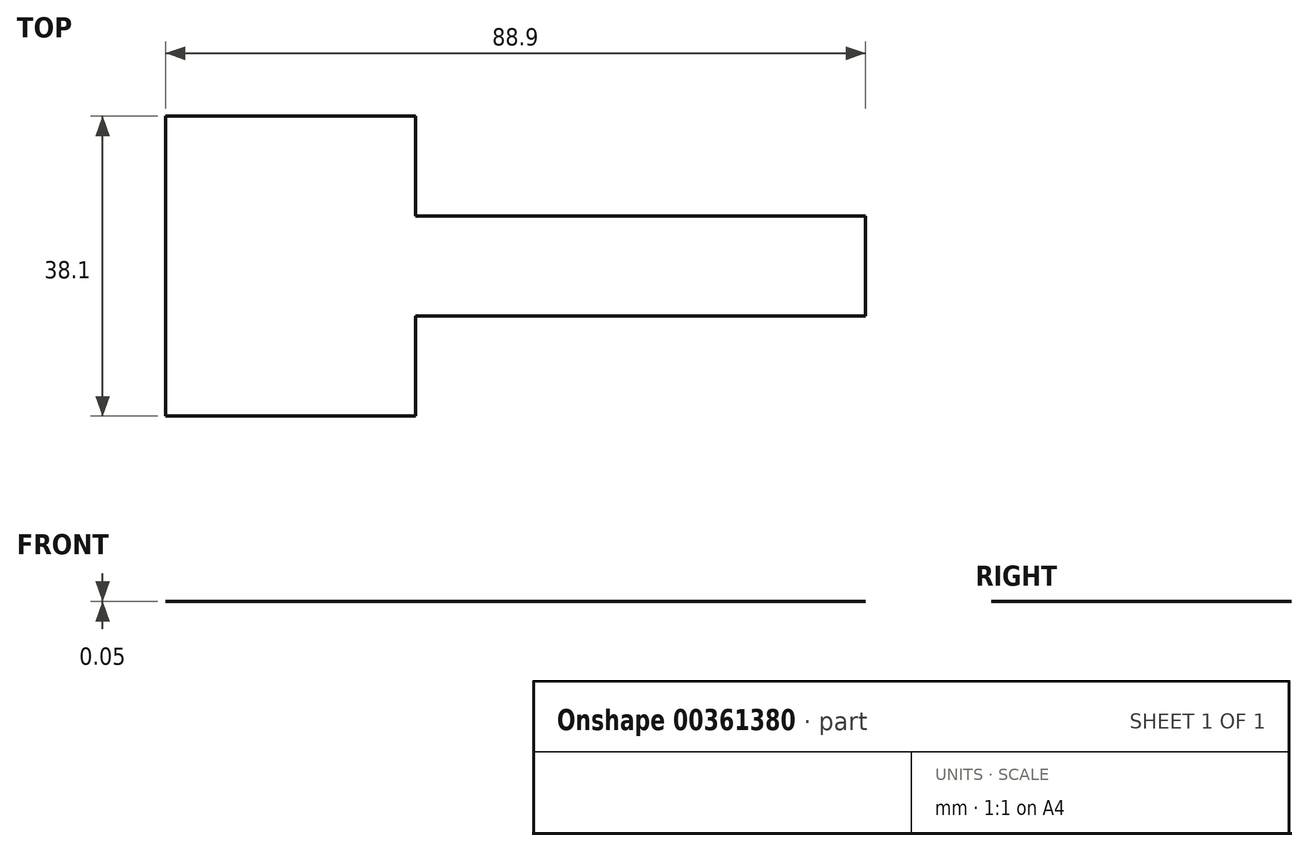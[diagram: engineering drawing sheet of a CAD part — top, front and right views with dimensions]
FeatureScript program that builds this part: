
annotation { "Feature Type Name" : "Feature", "Feature Type Description" : "" }
export const myFeature = defineFeature(function(context is Context, id is Id, definition is map)
    precondition{}
    {
        {
            var Q0;
            Q0=qCreatedBy(makeId("Top.planeOp"),FACE);
            var sketch = newSketch(context, id + "F0", { "sketchPlane" : qUnion([Q0])});
            skLineSegment(sketch, "E0", {"start": v(-91.66, -16.6) * mm, "end": v(-91.66, -54.7) * mm});
            skLineSegment(sketch, "E1", {"start": v(-91.66, -54.7) * mm, "end": v(-59.91, -54.7) * mm});
            skLineSegment(sketch, "E2", {"start": v(-59.91, -54.7) * mm, "end": v(-59.91, -42) * mm});
            skLineSegment(sketch, "E3", {"start": v(-59.91, -42) * mm, "end": v(-2.76, -42) * mm});
            skLineSegment(sketch, "E4", {"start": v(-2.76, -42) * mm, "end": v(-2.76, -29.3) * mm});
            skLineSegment(sketch, "E5", {"start": v(-2.76, -29.3) * mm, "end": v(-59.91, -29.3) * mm});
            skLineSegment(sketch, "E6", {"start": v(-59.91, -29.3) * mm, "end": v(-59.91, -16.6) * mm});
            skLineSegment(sketch, "E7", {"start": v(-59.91, -16.6) * mm, "end": v(-91.66, -16.6) * mm});
            skSolve(sketch);
        }
        {
            var Q0;
            Q0 = qSketchRegion(id + "F0", true);
            extrude(context, id + "F1", {"entities" : qUnion([Q0]), "depth" : 5 / 101.6 * mm});
        }
        {
            var Q0;
            Q0=makeQuery(id+"F1.opExtrude","SWEPT_FACE",FACE,{"disambiguationData":[OSD([sQuery(id+"F0.wireOp",EDGE,"E1")])]});
            var sketch = newSketch(context, id + "F2", { "sketchPlane" : qUnion([Q0])});
            skLineSegment(sketch, "E8", {"start": v(-59.91, 0) * mm, "end": v(-74.42, 31.75) * mm});
            skLineSegment(sketch, "E9", {"start": v(-74.42, 31.75) * mm, "end": v(-59.91, 44.04) * mm});
            skLineSegment(sketch, "E10", {"start": v(-59.91, 44.04) * mm, "end": v(-48.71, 44.04) * mm});
            skLineSegment(sketch, "E11", {"start": v(-48.71, 44.04) * mm, "end": v(-48.71, 10.05) * mm});
            skLineSegment(sketch, "E12", {"start": v(-47.29, 10.05) * mm, "end": v(-59.91, 0) * mm});
            skSolve(sketch);
        }
        {
            var Q0;
            {var subQ0=sQuery(id+"F2.wireOp",EDGE,"E8");Q0=makeQuery(id+"F2.imprint","IMPRINT",FACE,{"disambiguationData":[TD([[makeQuery(id+"F2.imprint","IMPRINT",EDGE,{"derivedFrom":subQ0}),-1.0]])]});}
            extrude(context, id + "F3", {"entities" : qUnion([Q0]), "operationType" : NewBodyOperationType.REMOVE, "depth" : 25.4 * mm});
        }
        {
            var Q0;
            Q0=makeQuery(id+"F1.opExtrude","SWEPT_FACE",FACE,{"disambiguationData":[OSD([sQuery(id+"F0.wireOp",EDGE,"E1")])]});
            var sketch = newSketch(context, id + "F4", { "sketchPlane" : qUnion([Q0])});
            skLineSegment(sketch, "E13", {"start": v(-59.91, 0) * mm, "end": v(-75.79, 31.75) * mm});
            skLineSegment(sketch, "E14", {"start": v(-75.79, 31.75) * mm, "end": v(-62.04, 45.95) * mm});
            skLineSegment(sketch, "E15", {"start": v(-62.04, 45.95) * mm, "end": v(-46.33, 45.95) * mm});
            skLineSegment(sketch, "E16", {"start": v(-46.33, 45.95) * mm, "end": v(-46.33, 12.06) * mm});
            skLineSegment(sketch, "E17", {"start": v(-59.91, 0) * mm, "end": v(-46.33, 12.06) * mm});
            skSolve(sketch);
        }
        {
            var Q0;
            Q0 = qSketchRegion(id + "F4", true);
            extrude(context, id + "F5", {"entities" : qUnion([Q0]), "operationType" : NewBodyOperationType.REMOVE, "oppositeDirection" : true, "depth" : 12.7 * mm});
        }
        {
            var Q0;
            Q0=makeQuery(id+"F1.opExtrude","SWEPT_FACE",FACE,{"disambiguationData":[OSD([sQuery(id+"F0.wireOp",EDGE,"E7")])]});
            var sketch = newSketch(context, id + "F6", { "sketchPlane" : qUnion([Q0])});
            skLineSegment(sketch, "E18", {"start": v(72.61, 31.75) * mm, "end": v(59.91, 0) * mm});
            skSolve(sketch);
        }
        {
            var Q0;
            Q0 = qSketchRegion(id + "F6", true);
            var Q1;
            {var subQ0=sQuery(id+"F6.wireOp",EDGE,"E18");Q1=makeQuery(id+"F6.imprint","IMPRINT",FACE,{"disambiguationData":[TD([[makeQuery(id+"F6.imprint","IMPRINT",EDGE,{"derivedFrom":subQ0}),-1.0]])]});}
            extrude(context, id + "F7", {"entities" : qUnion([Q0, Q1]), "operationType" : NewBodyOperationType.REMOVE, "oppositeDirection" : true, "depth" : 12.7 * mm});
        }
        {
            var Q0;
            Q0=makeQuery(id+"F5.boolean.opBoolean","MERGE",FACE,{"derivedFrom":[makeQuery(id+"F1.opExtrude","SWEPT_FACE",FACE,{"disambiguationData":[OSD([sQuery(id+"F0.wireOp",EDGE,"E3")])]}),makeQuery(id+"F5.opExtrude","CAP_FACE",FACE,{"disambiguationData":[OSD([sQuery(id+"F4.wireOp",EDGE,"E13"),sQuery(id+"F4.wireOp",EDGE,"E14"),sQuery(id+"F4.wireOp",EDGE,"E15"),sQuery(id+"F4.wireOp",EDGE,"E16"),sQuery(id+"F4.wireOp",EDGE,"E17")])],"isStart":false})]});
            var sketch = newSketch(context, id + "F8", { "sketchPlane" : qUnion([Q0])});
            skLineSegment(sketch, "E19", {"start": v(-2.76, 0) * mm, "end": v(-15.46, 31.75) * mm});
            skSolve(sketch);
        }
        {
            var Q0;
            Q0 = qSketchRegion(id + "F8", true);
            var Q1;
            {var subQ0=sQuery(id+"F8.wireOp",EDGE,"E19");Q1=makeQuery(id+"F8.imprint","IMPRINT",FACE,{"disambiguationData":[TD([[makeQuery(id+"F8.imprint","IMPRINT",EDGE,{"derivedFrom":subQ0}),-1.0]])]});}
            extrude(context, id + "F9", {"entities" : qUnion([Q0, Q1]), "operationType" : NewBodyOperationType.REMOVE, "oppositeDirection" : true, "depth" : 12.7 * mm});
        }
    });
